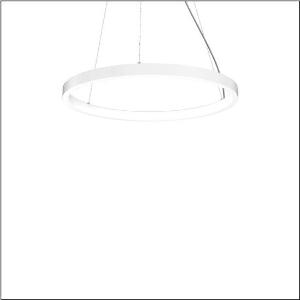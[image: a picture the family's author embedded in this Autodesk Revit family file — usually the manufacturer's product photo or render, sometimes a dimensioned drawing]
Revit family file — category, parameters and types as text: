
# Revit family: silica_21_ring-i_5pjbi3d1004a
name_source: partatom
category: Lighting Fixtures
units: mm (PartAtom-declared; Revit-internal decimal feet)

## family parameters
Cut with Voids When Loaded = No
Host = Face
Light Source = No
Part Type = Normal
Room Calculation Point = No
Round Connector Dimension = Use Diameter
Shared = No

## types (1)
- Silica 21 Ring-I (1 x LED, 6120 lm, 105 W, 3000K)
    Apparent Load = 105 VA
    CIE Flux Codes = 22 48 76 50 101
    Color Rendering = 80
    Color Temperature = 3000K
    Default Elevation = 1800 mm
    Description = Silica 21 Ring-I, suspended luminaire, of PMMA, frosted, light emission: inner ring side luminous distribution, primary light characteristic: symmetric, installation type: suspended mounting, LED, rated luminous flux: 6.120lm, luminous efficacy: 58lm/W, light colour: 830, colour temperature: 3000K, control gear: DALI 2, with terminal, 5-pole, mains connection: 230V, AC/DC, 0/50..60Hz, rated input power: 105W, housing, of extruded aluminium section, traffic white (RAL 9016), diameter: 1.090mm, ceiling canopy, traffic white (RAL 9016), protection rating (lamp compartment): IP40, insulation class (complete): insulation class I (protective earthing), certification: CE, impact resistance: IK02, permissible operating ambient temperature: 0..+35°C, packaging unit: 1 piece
    Height = 48 mm  [stored 0.15748 ft]
    Lamp = 1 x LED
    Lamp Light Flux = 6120 lm
    Lamp Power = 105 W
    Lamp count = 1
    Length = 1090 mm
    Luminous efficacy = 58 lm/W
    Manufacturer = Siteco
    ModVariant = No
    Model = 5PJBI3D1004A
    Mounting Place = Ceiling
    Mounting Type = Pendant
    Number of Poles = 1
    OnlyDefault = Yes
    Power Factor = 1
    Product Name = Silica 21 Ring-I
    Product group = suspended luminaire
    ProductGroupID = 904
    Protection Class = Protection class I
    Protection Degree = IP 40
    RLX_Detail_Level = 1
    RLX_Emergency_Light_Flux = 0 lm
    RLX_Emergency_Type = 0
    RLX_Emergency_Type_DB = No
    RlxData = <blob elided: 12789 chars, md5=658f8670>
    Socket = socket
    Standby Power = 0 W
    System Light Flux = 6120 lm
    System Power = 105 W
    Type Comments = Product without accessories
    Type Image = l_1258371.jpg
    URL = http://relux.com
    VarID = ---
    Voltage = 0 V
    Weight = 0.00 kg
    Width = 0 mm  [stored 0 ft]

note: [stored X ft] marks values corroborated as IEEE doubles in the binary element streams (Revit-internal decimal feet)

## geometry (parser evidence)
native form markers: Sweep x12
no freeform markers — native parametric forms only
